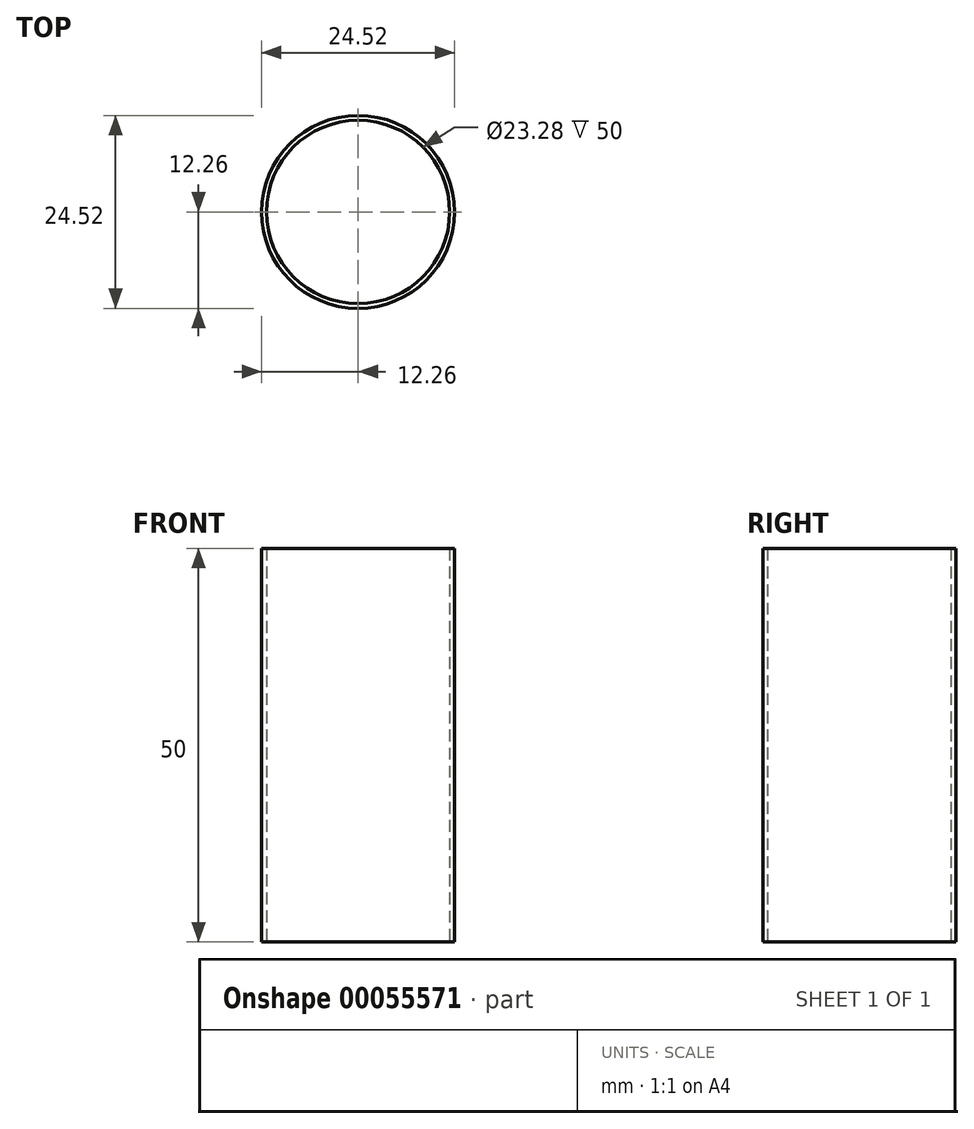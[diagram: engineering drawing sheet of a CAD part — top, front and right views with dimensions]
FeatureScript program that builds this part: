
annotation { "Feature Type Name" : "Feature", "Feature Type Description" : "" }
export const myFeature = defineFeature(function(context is Context, id is Id, definition is map)
    precondition{}
    {
        {
            var Q0;
            Q0=qCreatedBy(makeId("Top.planeOp"),FACE);
            var sketch = newSketch(context, id + "F0", { "sketchPlane" : qUnion([Q0])});
            skCircle(sketch, "E0", {"center": v(0, 0) * mm, "radius": 11.64 * mm});
            skCircle(sketch, "E1", {"center": v(0, 0) * mm, "radius": 12.26 * mm});
            skSolve(sketch);
        }
        {
            var Q0;
            Q0=makeQuery(id+"F0.imprint","IMPRINT",FACE,{"disambiguationData":[TD([[makeQuery(id+"F0.imprint","IMPRINT",EDGE,{"derivedFrom":sQuery(id+"F0.wireOp",EDGE,"E0")}),-1.0]])]});
            extrude(context, id + "F1", {"entities" : qUnion([Q0]), "depth" : 50 * mm});
        }
    });
